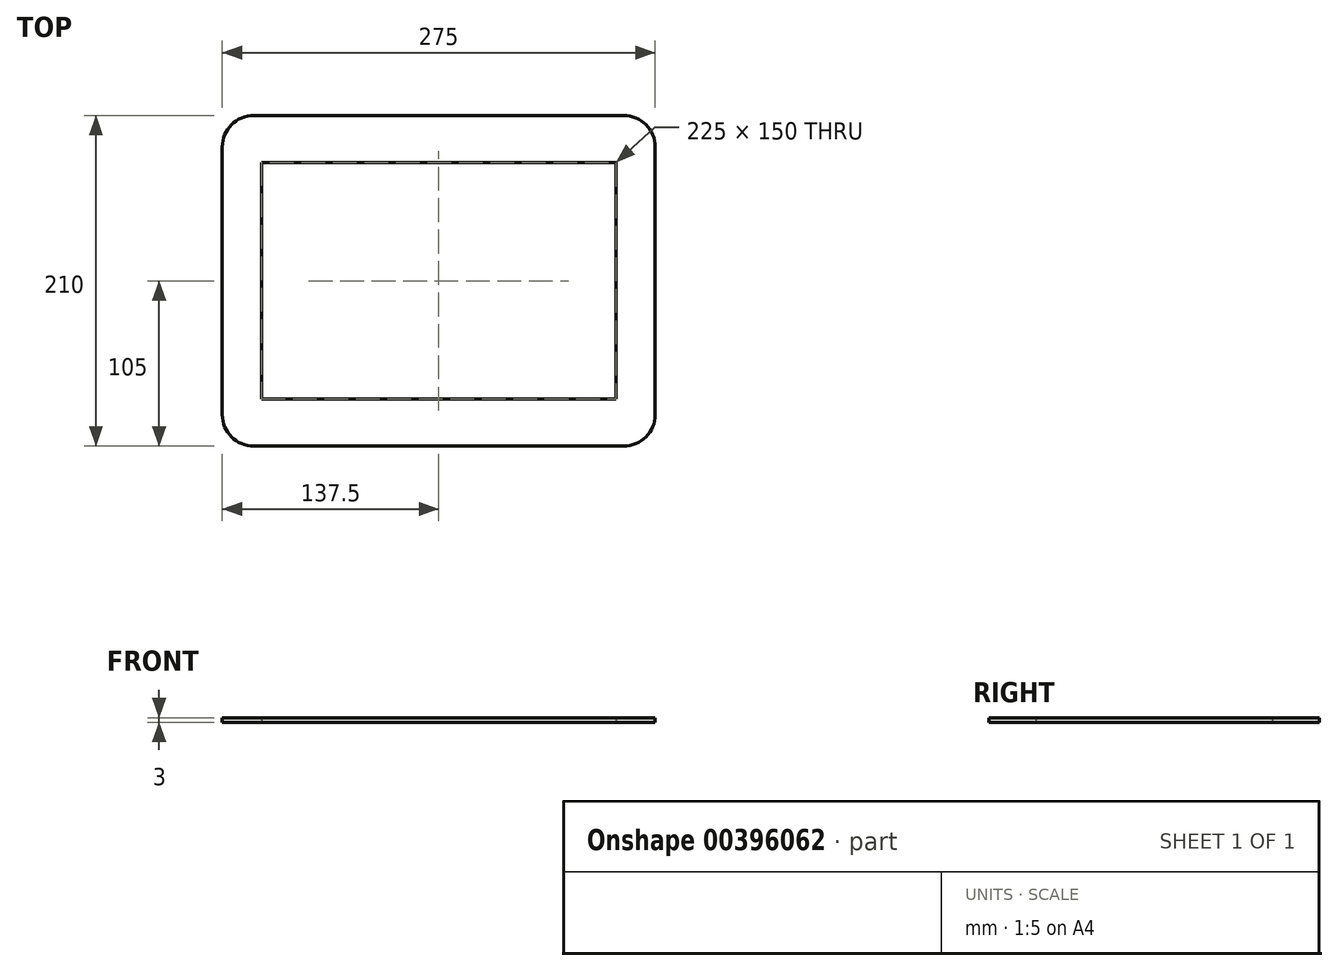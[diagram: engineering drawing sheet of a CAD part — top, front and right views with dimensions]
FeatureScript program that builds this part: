
annotation { "Feature Type Name" : "Feature", "Feature Type Description" : "" }
export const myFeature = defineFeature(function(context is Context, id is Id, definition is map)
    precondition{}
    {
        {
            var Q0;
            Q0=qCreatedBy(makeId("Top.planeOp"),FACE);
            var sketch = newSketch(context, id + "F0", { "sketchPlane" : qUnion([Q0])});
            skLineSegment(sketch, "E0.bottom", {"start": v(-117.5, 105) * mm, "end": v(117.5, 105) * mm});
            skLineSegment(sketch, "E0.top", {"start": v(-117.5, -105) * mm, "end": v(117.5, -105) * mm});
            skLineSegment(sketch, "E0.left", {"start": v(-137.5, 85) * mm, "end": v(-137.5, -85) * mm});
            skLineSegment(sketch, "E0.right", {"start": v(137.5, 85) * mm, "end": v(137.5, -85) * mm});
            skPoint(sketch, "E0.middle", {"position": v(0, 0) * mm});
            skPoint(sketch, "E1.visualSharp", {"position": v(-137.5, 105) * mm});
            skArc(sketch, "E1.filletArc", {"start": v(-117.5, 105) * mm, "mid": v(-131.64, 99.14) * mm, "end": v(-137.5, 85) * mm});
            skPoint(sketch, "E2.visualSharp", {"position": v(-137.5, -105) * mm});
            skArc(sketch, "E2.filletArc", {"start": v(-137.5, -85) * mm, "mid": v(-131.64, -99.14) * mm, "end": v(-117.5, -105) * mm});
            skPoint(sketch, "E3.visualSharp", {"position": v(137.5, -105) * mm});
            skArc(sketch, "E3.filletArc", {"start": v(117.5, -105) * mm, "mid": v(131.64, -99.14) * mm, "end": v(137.5, -85) * mm});
            skPoint(sketch, "E4.visualSharp", {"position": v(137.5, 105) * mm});
            skArc(sketch, "E4.filletArc", {"start": v(137.5, 85) * mm, "mid": v(131.64, 99.14) * mm, "end": v(117.5, 105) * mm});
            skLineSegment(sketch, "E5.bottom", {"start": v(-112.5, 75) * mm, "end": v(112.5, 75) * mm});
            skLineSegment(sketch, "E5.top", {"start": v(-112.5, -75) * mm, "end": v(112.5, -75) * mm});
            skLineSegment(sketch, "E5.left", {"start": v(-112.5, 75) * mm, "end": v(-112.5, -75) * mm});
            skLineSegment(sketch, "E5.right", {"start": v(112.5, 75) * mm, "end": v(112.5, -75) * mm});
            skSolve(sketch);
        }
        {
            var Q0;
            Q0=qSketchRegion(id+"F0",true);
            extrude(context, id + "F1", {"entities" : qUnion([Q0]), "depth" : 3 * mm});
        }
    });
